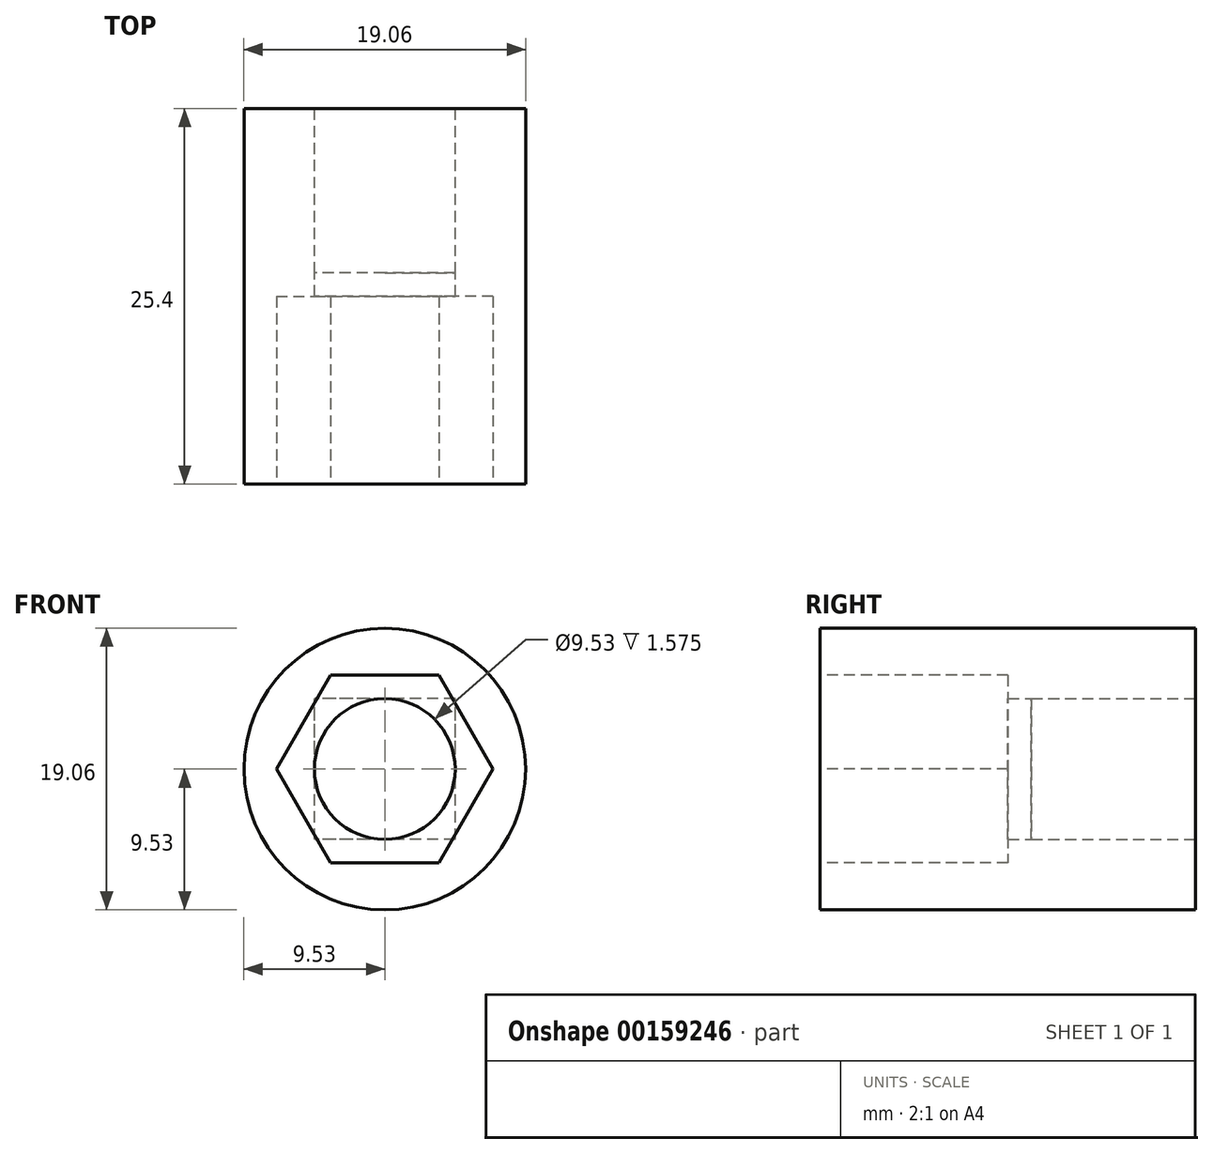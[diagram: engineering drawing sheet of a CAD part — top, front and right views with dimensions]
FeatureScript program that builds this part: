
annotation { "Feature Type Name" : "Feature", "Feature Type Description" : "" }
export const myFeature = defineFeature(function(context is Context, id is Id, definition is map)
    precondition{}
    {
        {
            var Q0;
            Q0=qCreatedBy(makeId("Front.planeOp"),FACE);
            var sketch = newSketch(context, id + "F0", { "sketchPlane" : qUnion([Q0])});
            skCircle(sketch, "E0", {"center": v(0, 0) * mm, "radius": 9.53 * mm});
            skSolve(sketch);
        }
        {
            var Q0;
            Q0 = qSketchRegion(id + "F0", true);
            extrude(context, id + "F1", {"entities" : qUnion([Q0]), "depth" : 25.4 * mm});
        }
        {
            var Q0;
            Q0=qCreatedBy(makeId("Front.planeOp"),FACE);
            var sketch = newSketch(context, id + "F2", { "sketchPlane" : qUnion([Q0])});
            skLineSegment(sketch, "E1.bottom", {"start": v(4.76, -4.76) * mm, "end": v(-4.76, -4.76) * mm});
            skLineSegment(sketch, "E1.top", {"start": v(4.76, 4.76) * mm, "end": v(-4.76, 4.76) * mm});
            skLineSegment(sketch, "E1.left", {"start": v(4.76, -4.76) * mm, "end": v(4.76, 4.76) * mm});
            skLineSegment(sketch, "E1.right", {"start": v(-4.76, -4.76) * mm, "end": v(-4.76, 4.76) * mm});
            skPoint(sketch, "E1.middle", {"position": v(0, 0) * mm});
            skCircle(sketch, "E2", {"center": v(0, 0) * mm, "radius": 4.76 * mm});
            skSolve(sketch);
        }
        {
            var Q0;
            {var subQ0=sQuery(id+"F2.wireOp",EDGE,"E2");var subQ1=makeQuery(id+"F2.imprint","INTERSECT",VERTEX,{"derivedFrom":[sQuery(id+"F2.wireOp",EDGE,"E1.top"),subQ0]});Q0=makeQuery(id+"F2.imprint","IMPRINT",FACE,{"disambiguationData":[TD([[makeQuery(id+"F2.imprint","IMPRINT",EDGE,{"disambiguationData":[TD([[subQ1,1.0]])],"derivedFrom":subQ0}),1.0]])]});}
            var Q1;
            Q1=sQuery(id+"F2.wireOp",EDGE,"E2");
            extrude(context, id + "F3", {"entities" : qUnion([Q0]), "operationType" : NewBodyOperationType.REMOVE, "surfaceEntities" : qUnion([Q1]), "endBound" : BoundingType.THROUGH_ALL, "depth" : 25.4 * mm});
        }
        {
            var Q0;
            {var subQ0=sQuery(id+"F2.wireOp",EDGE,"E1.left");var subQ1=sQuery(id+"F2.wireOp",EDGE,"E1.top");var subQ2=makeQuery(id+"F2.imprint","INTERSECT",VERTEX,{"derivedFrom":[subQ1,subQ0]});Q0=makeQuery(id+"F2.imprint","IMPRINT",FACE,{"disambiguationData":[TD([[makeQuery(id+"F2.imprint","IMPRINT",EDGE,{"disambiguationData":[TD([[subQ2,-1.0]])],"derivedFrom":subQ1}),1.0]])]});}
            var Q1;
            {var subQ0=sQuery(id+"F2.wireOp",EDGE,"E1.right");var subQ1=sQuery(id+"F2.wireOp",EDGE,"E1.top");var subQ2=makeQuery(id+"F2.imprint","INTERSECT",VERTEX,{"derivedFrom":[subQ1,subQ0]});Q1=makeQuery(id+"F2.imprint","IMPRINT",FACE,{"disambiguationData":[TD([[makeQuery(id+"F2.imprint","IMPRINT",EDGE,{"disambiguationData":[TD([[subQ2,1.0]])],"derivedFrom":subQ1}),1.0]])]});}
            var Q2;
            {var subQ0=sQuery(id+"F2.wireOp",EDGE,"E1.right");var subQ1=sQuery(id+"F2.wireOp",EDGE,"E1.bottom");var subQ2=makeQuery(id+"F2.imprint","INTERSECT",VERTEX,{"derivedFrom":[subQ1,subQ0]});Q2=makeQuery(id+"F2.imprint","IMPRINT",FACE,{"disambiguationData":[TD([[makeQuery(id+"F2.imprint","IMPRINT",EDGE,{"disambiguationData":[TD([[subQ2,1.0]])],"derivedFrom":subQ1}),-1.0]])]});}
            var Q3;
            {var subQ0=sQuery(id+"F2.wireOp",EDGE,"E1.left");var subQ1=sQuery(id+"F2.wireOp",EDGE,"E1.bottom");var subQ2=makeQuery(id+"F2.imprint","INTERSECT",VERTEX,{"derivedFrom":[subQ1,subQ0]});Q3=makeQuery(id+"F2.imprint","IMPRINT",FACE,{"disambiguationData":[TD([[makeQuery(id+"F2.imprint","IMPRINT",EDGE,{"disambiguationData":[TD([[subQ2,-1.0]])],"derivedFrom":subQ1}),-1.0]])]});}
            extrude(context, id + "F4", {"entities" : qUnion([Q0, Q1, Q2, Q3]), "operationType" : NewBodyOperationType.REMOVE, "depth" : 11.13 * mm});
        }
        {
            var Q0;
            Q0=makeQuery(id+"F1.opExtrude","CAP_FACE",FACE,{"disambiguationData":[OSD([sQuery(id+"F0.wireOp",EDGE,"E0")])],"isStart":false});
            var sketch = newSketch(context, id + "F5", { "sketchPlane" : qUnion([Q0])});
            skCircle(sketch, "E3.cCircle", {"center": v(0, 0) * mm, "radius": 6.35 * mm, "construction": true});
            skLineSegment(sketch, "E3.0", {"start": v(7.33, 0) * mm, "end": v(3.67, -6.35) * mm});
            skLineSegment(sketch, "E3.1", {"start": v(3.67, -6.35) * mm, "end": v(-3.67, -6.35) * mm});
            skLineSegment(sketch, "E3.2", {"start": v(-3.67, -6.35) * mm, "end": v(-7.33, 0) * mm});
            skLineSegment(sketch, "E3.3", {"start": v(-7.33, 0) * mm, "end": v(-3.67, 6.35) * mm});
            skLineSegment(sketch, "E3.4", {"start": v(-3.67, 6.35) * mm, "end": v(3.67, 6.35) * mm});
            skLineSegment(sketch, "E3.5", {"start": v(3.67, 6.35) * mm, "end": v(7.33, 0) * mm});
            skPoint(sketch, "E3.0.midPoint", {"position": v(5.5, -3.18) * mm});
            skSolve(sketch);
        }
        {
            var Q0;
            Q0=makeQuery(id+"F5.imprint","IMPRINT",FACE,{"disambiguationData":[TD([[makeQuery(id+"F5.imprint","IMPRINT",EDGE,{"derivedFrom":sQuery(id+"F5.wireOp",EDGE,"E3.0")}),-1.0]])]});
            extrude(context, id + "F6", {"entities" : qUnion([Q0]), "operationType" : NewBodyOperationType.REMOVE, "oppositeDirection" : true, "depth" : 12.7 * mm});
        }
    });
